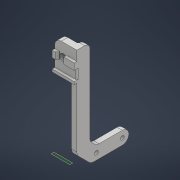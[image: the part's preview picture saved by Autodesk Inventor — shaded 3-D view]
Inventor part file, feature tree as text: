
AUTODESK INVENTOR PART (.ipt)
format: ipt  version: 2021 (Build 250183000, 183)  size: 416,768 bytes
history: native  units: mm
features: sketch x15, extrude x11, fillet x8, move_body x8, projected_geometry x7, direct_edit x5, hole x4, chamfer x3, draft x2, plane x1, split x1, mirror x1
ambient origin geometry x8: Origin, YZ Plane, XZ Plane, XY Plane, X Axis, Y Axis, Z Axis, Center Point
bodies: Solid1 (feature_tree)
feature tree (66):
  extrude  "Extrusion1"  Depth=10.0mm
  hole  "Hole1"  [1 undecoded]
  draft  "FaceDraft1"
  extrude  "Extrusion2"  Depth=10.0mm TaperAngle=0.0deg
  fillet  "Fillet2"  Radius=0.5mm
  extrude  "Extrusion3"  Depth=20.0mm
  extrude  "Extrusion4"  Depth=5.0mm
  extrude  "Extrusion5"  Depth=5.1mm
  extrude  "Extrusion6"  Depth=2.0mm TaperAngle=0.0deg
  fillet  "Fillet4"  Radius=1.0mm
  chamfer  "Chamfer1"  Distance=1.0mm
  direct_edit  "Direct Edit2"
  plane  "Work Plane1"
  split  "Split1"
  extrude  "Extrusion7"  Depth=2.0mm TaperAngle=45.0deg
  hole  "Hole2"  [1 undecoded]
  direct_edit  "Direct Edit3"
  draft  "FaceDraft2"
  fillet  "Fillet5"  Radius=55.0mm
  direct_edit  "Direct Edit5"
  fillet  "Fillet7"  Radius=36.0mm
  fillet  "Fillet8"  Radius=30.0mm
  extrude  "Extrusion8"  Depth=20.0mm
  direct_edit  "Direct Edit6"
  extrude  "Extrusion9"  Depth=5.0mm
  fillet  "Fillet9"  Radius=5.0mm
  fillet  "Fillet10"  Radius=5.0mm
  mirror  "Mirror1"
  extrude  "Extrusion10"  Depth=10.0mm TaperAngle=0.0deg
  extrude  "Extrusion11"  Depth=4.363323mm
  chamfer  "Chamfer2"  Distance=1.0mm
  chamfer  "Chamfer3"  Distance=8.0mm
  hole  "Hole3"  [1 undecoded]
  direct_edit  "Direct Edit7"
  hole  "Hole4"  [1 undecoded]
  fillet  "Fillet11"  Radius=4.0mm
  sketch  "Sketch1"  dims[d3=5.0mm d4=0.0mm d5=10.0mm]
  sketch  "Sketch2"  dims[d6=5.1mm d7=6.0mm d8=4.0mm d9=2.0mm d10=90.0deg d11=8.0mm d12=20.594885mm d14=15.0deg]
  sketch  "Sketch3"  dims[d15=0.6mm d16=10.0mm d17=0.0mm d18=0.5mm]
  sketch  "Sketch4"  dims[d19=10.0mm d21=20.0mm]
  sketch  "Sketch5"  dims[d22=2.0mm d23=5.0mm]
  projected_geometry  "Projected Loop1"
  sketch  "Sketch6"  dims[d24=2.0mm d25=0.0mm d26=5.1mm]
  projected_geometry  "Projected Loop2"
  projected_geometry  "Projected Loop3"
  sketch  "Sketch7"  dims[d27=5.1mm d28=2.0mm d29=0.0mm d32=1.0mm d33=0.0mm d34=1.0mm d35=0.0mm]
  projected_geometry  "Projected Loop4"
  projected_geometry  "Projected Loop5"
  sketch  "Sketch8"  dims[d36=1.0mm d40=1.5mm d41=2.0mm d42=45.0deg]
  sketch  "Sketch9"  dims[d43=0.0mm d44=0.0mm d45=0.5mm d46=0.0mm d47=0.0mm d48=0.5mm d49=55.0mm d50=36.0mm d51=30.0mm]
  sketch  "Sketch10"  dims[d52=3.0mm d53=0.0mm d54=20.0mm]
  projected_geometry  "Projected Loop6"
  sketch  "Sketch11"  dims[d55=5.0mm d56=5.0mm d57=5.0mm d58=5.0mm]
  projected_geometry  "Projected Loop7"
  sketch  "Sketch13"  dims[d59=3.0mm d60=6.0mm d61=4.0mm d62=2.0mm d63=90.0deg d64=8.0mm d65=20.594885mm d66=0.0mm d67=0.0mm d68=10.0mm]
  sketch  "Sketch14"  dims[d69=0.0mm d70=0.0mm d71=-5.0mm d72=4.363323mm]
  sketch  "Sketch15"  dims[d73=5.0mm]
  sketch  "Sketch16"  dims[d77=10.0mm d78=0.0mm d79=0.0mm d80=1.0mm d81=8.0mm d82=5.0mm d83=0.0mm d84=0.0mm d85=0.0mm d86=0.0mm d87=4.0mm d88=0.0mm d89=0.0mm d90=4.0mm d91=1.0mm d92=10.0mm d93=4.0mm d94=0.0mm d95=5.0mm d96=5.0mm d97=1.0mm d99=5.0mm d100=0.0mm d101=0.0mm d106=30.0mm d109=5.0mm d111=10.0mm d112=0.0mm d115=10.0mm d116=10.0mm d117=5.0mm d118=2.0mm d119=45.0deg d120=11.0mm d121=2.0mm d122=45.0deg d123=2.9mm d124=6.0mm d125=4.0mm d126=2.0mm d127=90.0deg d128=8.0mm d129=20.594885mm d130=0.0mm d131=0.0mm d132=10.0mm d133=20.0mm d134=2.9mm d135=6.0mm d136=4.0mm d137=2.0mm d138=90.0deg d139=8.0mm d140=20.594885mm d141=5.0mm]
  move_body  "Move2"
  move_body  "Move3"
  move_body  "Move4"
  move_body  "Move5"
  move_body  "Move6"
  move_body  "Move7"
  move_body  "Move8"
  move_body  "Move9"
note: 4 required parameter values undecoded (feature->parameter linkage not recoverable at this tier; creation-order binding heuristic only, values carry confidence <= 0.55)
